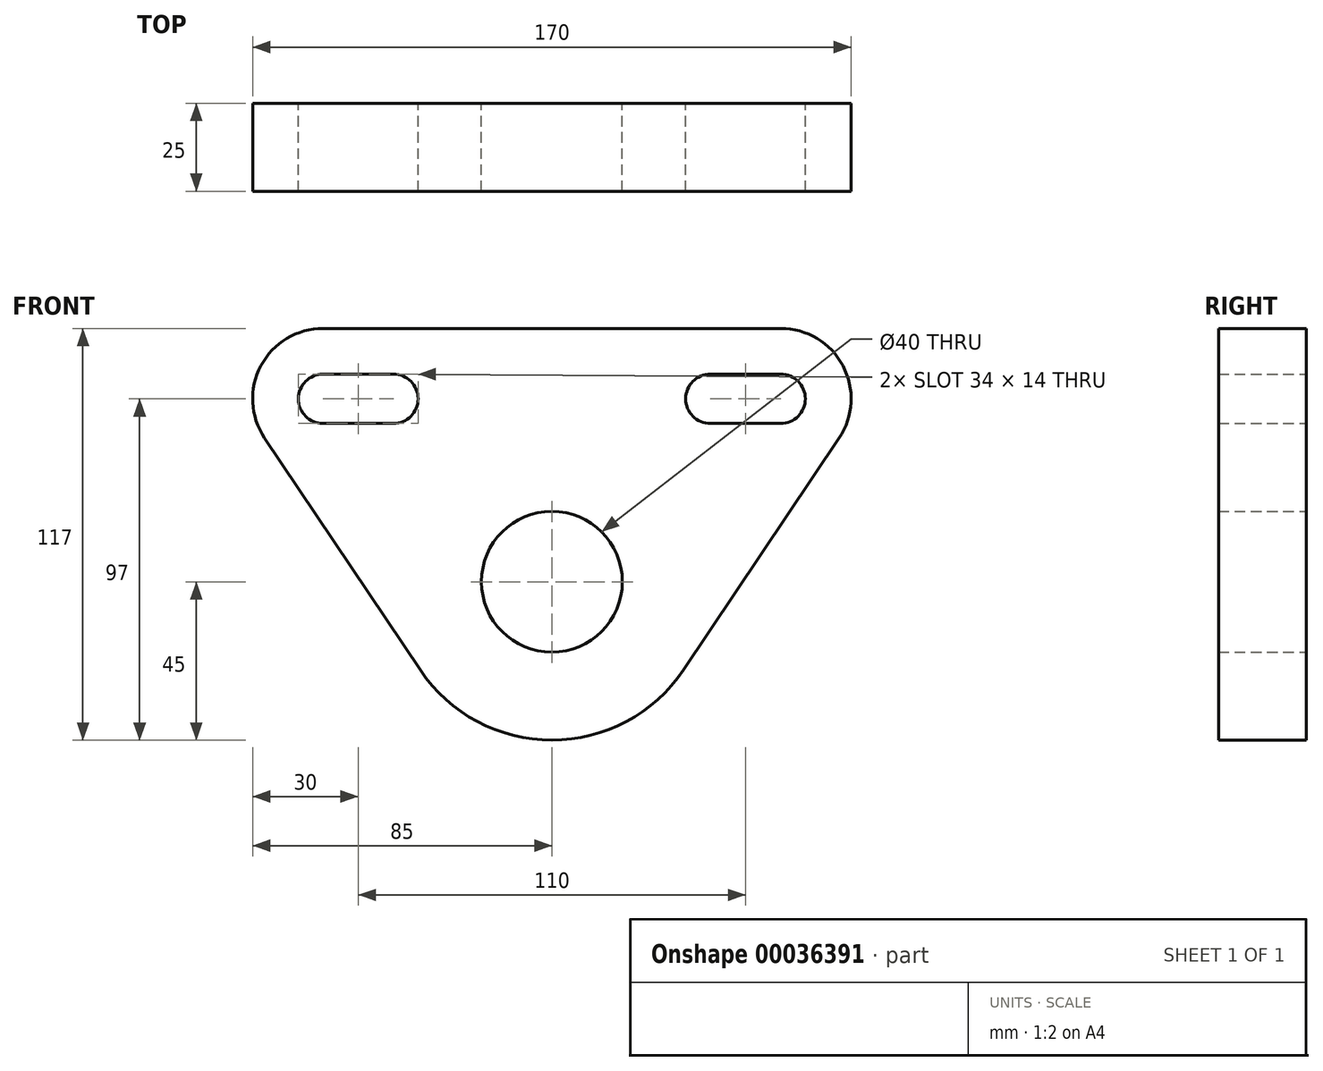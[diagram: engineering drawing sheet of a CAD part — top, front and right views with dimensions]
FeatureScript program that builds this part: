
annotation { "Feature Type Name" : "Feature", "Feature Type Description" : "" }
export const myFeature = defineFeature(function(context is Context, id is Id, definition is map)
    precondition{}
    {
        {
            var Q0;
            Q0=qCreatedBy(makeId("Front.planeOp"),FACE);
            var sketch = newSketch(context, id + "F0", { "sketchPlane" : qUnion([Q0])});
            skCircle(sketch, "E0", {"center": v(0, 0) * mm, "radius": 20 * mm});
            skArc(sketch, "E1", {"start": v(-37.37, -25.07) * mm, "mid": v(0, -45) * mm, "end": v(37.37, -25.07) * mm});
            skArc(sketch, "E2", {"start": v(-65, 72) * mm, "mid": v(-82.65, 61.41) * mm, "end": v(-81.6, 40.86) * mm});
            skArc(sketch, "E3", {"start": v(81.6, 40.86) * mm, "mid": v(82.65, 61.41) * mm, "end": v(65, 72) * mm});
            skLineSegment(sketch, "E4", {"start": v(-81.6, 40.86) * mm, "end": v(-37.37, -25.07) * mm});
            skLineSegment(sketch, "E5", {"start": v(-65, 72) * mm, "end": v(65, 72) * mm});
            skLineSegment(sketch, "E6", {"start": v(37.37, -25.07) * mm, "end": v(81.6, 40.86) * mm});
            skLineSegment(sketch, "E7.bottom", {"start": v(-65, 59) * mm, "end": v(-45, 59) * mm});
            skLineSegment(sketch, "E7.top", {"start": v(-65, 45) * mm, "end": v(-45, 45) * mm});
            skLineSegment(sketch, "E7.left", {"start": v(-72, 52) * mm, "end": v(-72, 52) * mm});
            skLineSegment(sketch, "E7.right", {"start": v(-38, 52) * mm, "end": v(-38, 52) * mm});
            skPoint(sketch, "E8.visualSharp", {"position": v(-72, 59) * mm});
            skArc(sketch, "E8.filletArc", {"start": v(-65, 59) * mm, "mid": v(-69.95, 56.95) * mm, "end": v(-72, 52) * mm});
            skPoint(sketch, "E9.visualSharp", {"position": v(-72, 45) * mm});
            skArc(sketch, "E9.filletArc", {"start": v(-72, 52) * mm, "mid": v(-69.95, 47.05) * mm, "end": v(-65, 45) * mm});
            skPoint(sketch, "E10.visualSharp", {"position": v(-38, 59) * mm});
            skArc(sketch, "E10.filletArc", {"start": v(-38, 52) * mm, "mid": v(-40.05, 56.95) * mm, "end": v(-45, 59) * mm});
            skPoint(sketch, "E11.visualSharp", {"position": v(-38, 45) * mm});
            skArc(sketch, "E11.filletArc", {"start": v(-45, 45) * mm, "mid": v(-40.05, 47.05) * mm, "end": v(-38, 52) * mm});
            skPoint(sketch, "E12.MirrorP", {"position": v(72, 45) * mm});
            skArc(sketch, "E13.MirrorCS", {"start": v(45, 45) * mm, "mid": v(40.05, 47.05) * mm, "end": v(38, 52) * mm});
            skArc(sketch, "E14.MirrorCS", {"start": v(38, 52) * mm, "mid": v(40.05, 56.95) * mm, "end": v(45, 59) * mm});
            skArc(sketch, "E15.MirrorCS", {"start": v(72, 52) * mm, "mid": v(69.95, 47.05) * mm, "end": v(65, 45) * mm});
            skPoint(sketch, "E16.MirrorP", {"position": v(38, 45) * mm});
            skPoint(sketch, "E17.MirrorP", {"position": v(72, 59) * mm});
            skLineSegment(sketch, "E18.MirrorCS", {"start": v(65, 59) * mm, "end": v(45, 59) * mm});
            skLineSegment(sketch, "E19.MirrorCS", {"start": v(65, 45) * mm, "end": v(45, 45) * mm});
            skArc(sketch, "E20.MirrorCS", {"start": v(65, 59) * mm, "mid": v(69.95, 56.95) * mm, "end": v(72, 52) * mm});
            skPoint(sketch, "E21.MirrorP", {"position": v(38, 59) * mm});
            skSolve(sketch);
        }
        {
            var Q0;
            Q0=makeQuery(id+"F0.imprint","IMPRINT",FACE,{"disambiguationData":[TD([[makeQuery(id+"F0.imprint","IMPRINT",EDGE,{"derivedFrom":sQuery(id+"F0.wireOp",EDGE,"E0")}),-1.0]])]});
            extrude(context, id + "F1", {"entities" : qUnion([Q0]), "depth" : 25 * mm});
        }
    });
